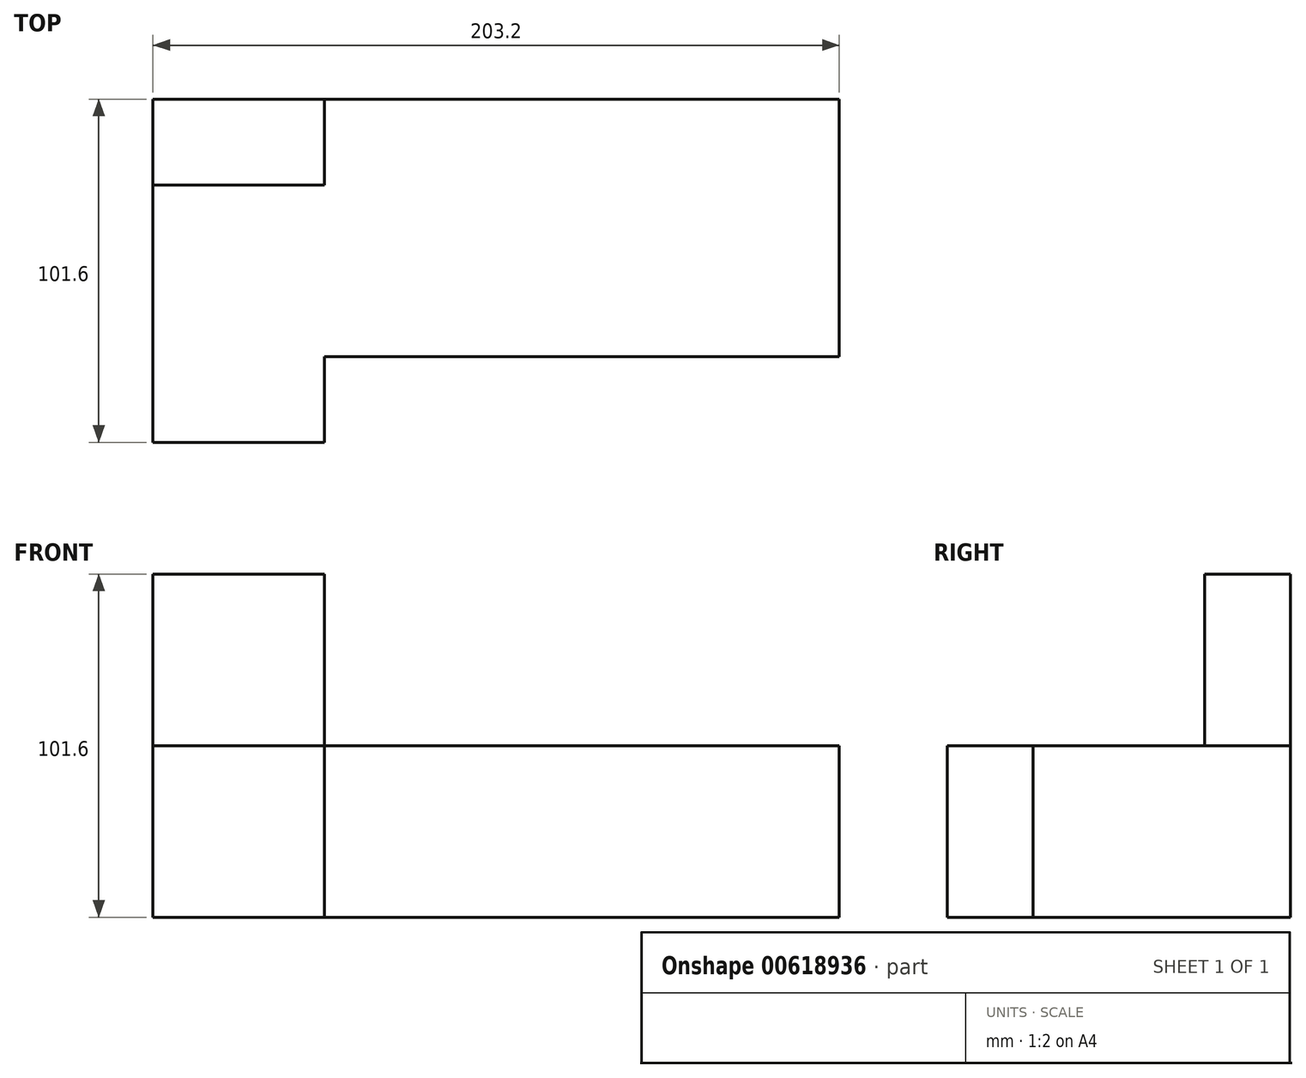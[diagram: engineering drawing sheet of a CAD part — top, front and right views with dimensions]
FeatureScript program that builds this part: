
annotation { "Feature Type Name" : "Feature", "Feature Type Description" : "" }
export const myFeature = defineFeature(function(context is Context, id is Id, definition is map)
    precondition{}
    {
        {
            var Q0;
            Q0=qCreatedBy(makeId("Top.planeOp"),FACE);
            var sketch = newSketch(context, id + "F0", { "sketchPlane" : qUnion([Q0])});
            skLineSegment(sketch, "E0.bottom", {"start": v(-97.43, -25.4) * mm, "end": v(-46.63, -25.4) * mm});
            skLineSegment(sketch, "E0.top", {"start": v(-97.43, 76.2) * mm, "end": v(105.77, 76.2) * mm});
            skLineSegment(sketch, "E0.left", {"start": v(-97.43, -25.4) * mm, "end": v(-97.43, 76.2) * mm});
            skLineSegment(sketch, "E0.right", {"start": v(105.77, 0) * mm, "end": v(105.77, 76.2) * mm});
            skLineSegment(sketch, "E1.top", {"start": v(105.77, 0) * mm, "end": v(-46.63, 0) * mm});
            skLineSegment(sketch, "E1.right", {"start": v(-46.63, -25.4) * mm, "end": v(-46.63, 0) * mm});
            skSolve(sketch);
        }
        {
            var Q0;
            Q0 = qSketchRegion(id + "F0", true);
            extrude(context, id + "F1", {"entities" : qUnion([Q0]), "depth" : 50.8 * mm, "offsetDistance" : 25.4 * mm});
        }
        {
            var Q0;
            Q0=makeQuery(id+"F1.opExtrude","CAP_FACE",FACE,{"disambiguationData":[OSD([sQuery(id+"F0.wireOp",EDGE,"E0.bottom"),sQuery(id+"F0.wireOp",EDGE,"E0.top"),sQuery(id+"F0.wireOp",EDGE,"E0.left"),sQuery(id+"F0.wireOp",EDGE,"E0.right"),sQuery(id+"F0.wireOp",EDGE,"E1.top"),sQuery(id+"F0.wireOp",EDGE,"E1.right")])],"isStart":false});
            var sketch = newSketch(context, id + "F2", { "sketchPlane" : qUnion([Q0])});
            skLineSegment(sketch, "E2.bottom", {"start": v(-97.43, 76.2) * mm, "end": v(-46.63, 76.2) * mm});
            skLineSegment(sketch, "E2.top", {"start": v(-97.43, 50.8) * mm, "end": v(-46.63, 50.8) * mm});
            skLineSegment(sketch, "E2.left", {"start": v(-97.43, 76.2) * mm, "end": v(-97.43, 50.8) * mm});
            skLineSegment(sketch, "E2.right", {"start": v(-46.63, 76.2) * mm, "end": v(-46.63, 50.8) * mm});
            skSolve(sketch);
        }
        {
            var Q0;
            Q0 = qSketchRegion(id + "F2", true);
            extrude(context, id + "F3", {"entities" : qUnion([Q0]), "operationType" : NewBodyOperationType.ADD, "depth" : 50.8 * mm, "offsetDistance" : 25.4 * mm});
        }
    });
